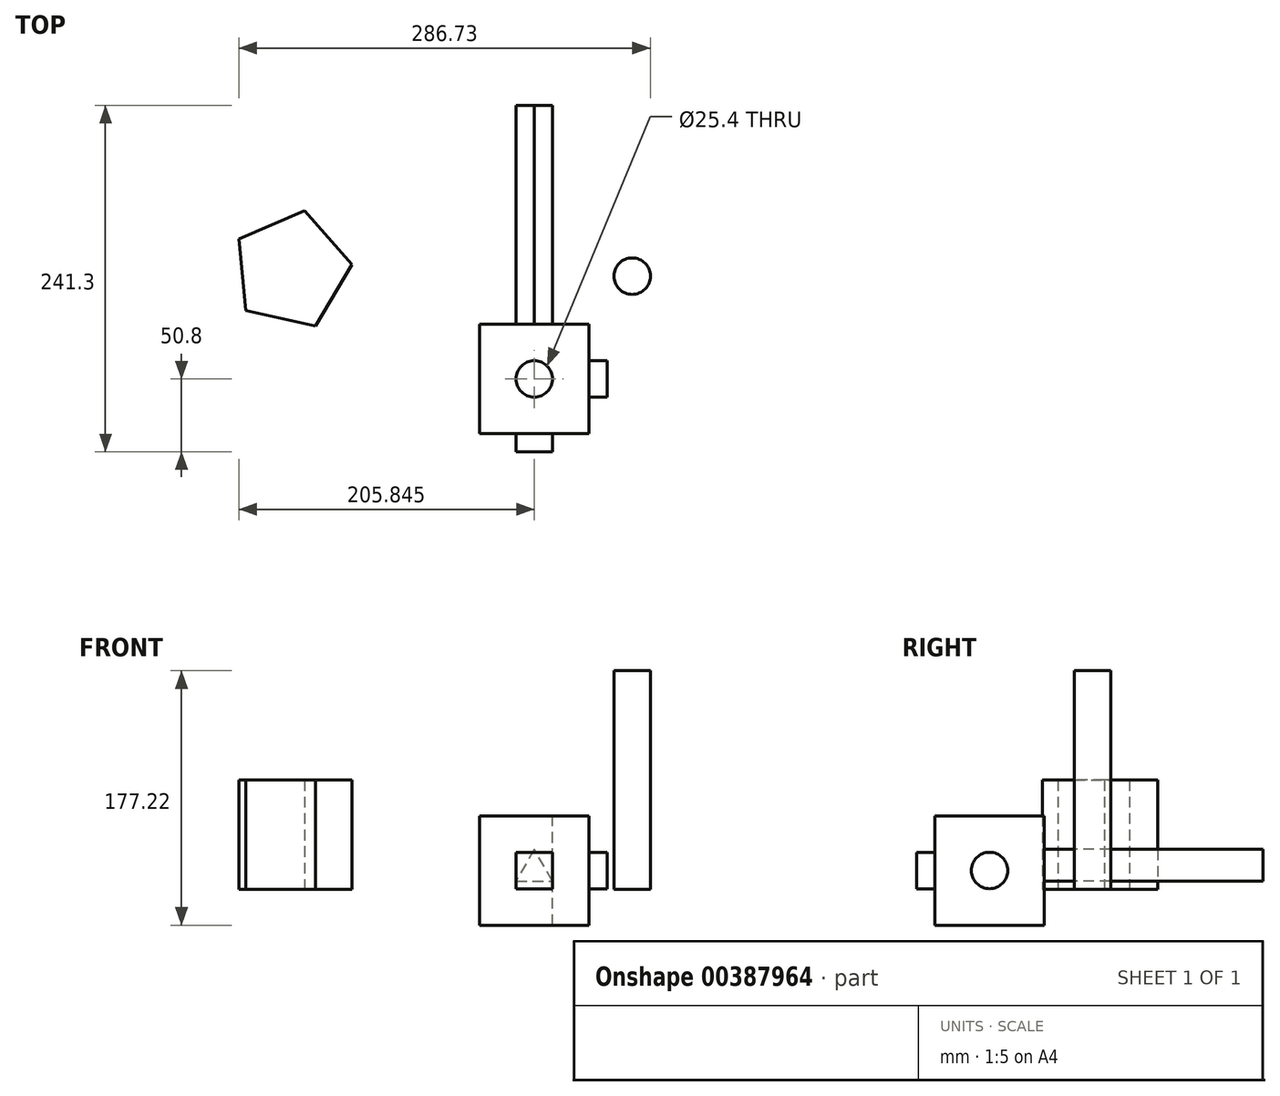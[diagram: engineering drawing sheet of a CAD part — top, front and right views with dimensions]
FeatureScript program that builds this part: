
annotation { "Feature Type Name" : "Feature", "Feature Type Description" : "" }
export const myFeature = defineFeature(function(context is Context, id is Id, definition is map)
    precondition{}
    {
        {
            var Q0;
            Q0=qCreatedBy(makeId("Front.planeOp"),FACE);
            var sketch = newSketch(context, id + "F0", { "sketchPlane" : qUnion([Q0])});
            skLineSegment(sketch, "E0.bottom", {"start": v(-38.89, -24.82) * mm, "end": v(37.31, -24.82) * mm});
            skLineSegment(sketch, "E0.top", {"start": v(-38.89, 51.38) * mm, "end": v(37.31, 51.38) * mm});
            skLineSegment(sketch, "E0.left", {"start": v(-38.89, -24.82) * mm, "end": v(-38.89, 51.38) * mm});
            skLineSegment(sketch, "E0.right", {"start": v(37.31, -24.82) * mm, "end": v(37.31, 51.38) * mm});
            skSolve(sketch);
        }
        {
            var Q0;
            Q0=makeQuery(id+"F0.imprint","IMPRINT",FACE,{"disambiguationData":[TD([[makeQuery(id+"F0.imprint","IMPRINT",EDGE,{"derivedFrom":sQuery(id+"F0.wireOp",EDGE,"E0.bottom")}),1.0]])]});
            extrude(context, id + "F1", {"entities" : qUnion([Q0]), "depth" : 76.2 * mm});
        }
        {
            var Q0;
            Q0=makeQuery(id+"F1.opExtrude","SWEPT_FACE",FACE,{"disambiguationData":[OSD([sQuery(id+"F0.wireOp",EDGE,"E0.top")])]});
            var sketch = newSketch(context, id + "F2", { "sketchPlane" : qUnion([Q0])});
            skPoint(sketch, "E1", {"position": v(-0.79, -38.1) * mm});
            skSolve(sketch);
        }
        {
            var Q0;
            Q0=sQuery(id+"F2.wireOp",VERTEX,"E1");
            var Q1;
            Q1=makeQuery(id+"F1.opExtrude","SWEPT_BODY",BODY,{"disambiguationData":[OSD([sQuery(id+"F0.wireOp",EDGE,"E0.bottom"),sQuery(id+"F0.wireOp",EDGE,"E0.top"),sQuery(id+"F0.wireOp",EDGE,"E0.left"),sQuery(id+"F0.wireOp",EDGE,"E0.right")])]});
            hole(context, id + "F3", {"style" : HoleStyle.SIMPLE, "endStyle" : HoleEndStyle.THROUGH, "holeDiameter" : 25.4 * mm, "isTappedThrough" : true, "tappedDepth" : 12.7 * mm, "tapClearance" : 3, "locations" : qUnion([Q0]), "scope" : qUnion([Q1])});
        }
        {
            var Q0;
            Q0=makeQuery(id+"F1.opExtrude","CAP_FACE",FACE,{"disambiguationData":[OSD([sQuery(id+"F0.wireOp",EDGE,"E0.bottom"),sQuery(id+"F0.wireOp",EDGE,"E0.top"),sQuery(id+"F0.wireOp",EDGE,"E0.left"),sQuery(id+"F0.wireOp",EDGE,"E0.right")])],"isStart":false});
            var sketch = newSketch(context, id + "F4", { "sketchPlane" : qUnion([Q0])});
            skLineSegment(sketch, "E2.bottom", {"start": v(-13.49, 0.58) * mm, "end": v(11.91, 0.58) * mm});
            skLineSegment(sketch, "E2.top", {"start": v(-13.49, 25.98) * mm, "end": v(11.91, 25.98) * mm});
            skLineSegment(sketch, "E2.left", {"start": v(-13.49, 0.58) * mm, "end": v(-13.49, 25.98) * mm});
            skLineSegment(sketch, "E2.right", {"start": v(11.91, 0.58) * mm, "end": v(11.91, 25.98) * mm});
            skSolve(sketch);
        }
        {
            var Q0;
            Q0=makeQuery(id+"F4.imprint","IMPRINT",FACE,{"disambiguationData":[TD([[makeQuery(id+"F4.imprint","IMPRINT",EDGE,{"derivedFrom":sQuery(id+"F4.wireOp",EDGE,"E2.bottom")}),1.0]])]});
            extrude(context, id + "F5", {"entities" : qUnion([Q0]), "operationType" : NewBodyOperationType.ADD, "depth" : 12.7 * mm});
        }
        {
            var Q0;
            Q0=makeQuery(id+"F1.opExtrude","SWEPT_FACE",FACE,{"disambiguationData":[OSD([sQuery(id+"F0.wireOp",EDGE,"E0.right")])]});
            var sketch = newSketch(context, id + "F6", { "sketchPlane" : qUnion([Q0])});
            skCircle(sketch, "E3", {"center": v(-38.1, 13.28) * mm, "radius": 12.7 * mm});
            skSolve(sketch);
        }
        {
            var Q0;
            Q0=makeQuery(id+"F6.imprint","IMPRINT",FACE,{"disambiguationData":[TD([[makeQuery(id+"F6.imprint","IMPRINT",EDGE,{"derivedFrom":sQuery(id+"F6.wireOp",EDGE,"E3")}),1.0]])]});
            extrude(context, id + "F7", {"entities" : qUnion([Q0]), "operationType" : NewBodyOperationType.ADD, "depth" : 12.7 * mm});
        }
        {
            var Q0;
            Q0=makeQuery(id+"F1.opExtrude","CAP_FACE",FACE,{"disambiguationData":[OSD([sQuery(id+"F0.wireOp",EDGE,"E0.bottom"),sQuery(id+"F0.wireOp",EDGE,"E0.top"),sQuery(id+"F0.wireOp",EDGE,"E0.left"),sQuery(id+"F0.wireOp",EDGE,"E0.right")])],"isStart":true});
            var sketch = newSketch(context, id + "F8", { "sketchPlane" : qUnion([Q0])});
            skCircle(sketch, "E4.cCircle", {"center": v(0.79, 13.28) * mm, "radius": 7.33 * mm, "construction": true});
            skLineSegment(sketch, "E4.0", {"start": v(-11.91, 5.95) * mm, "end": v(0.79, 27.94) * mm});
            skLineSegment(sketch, "E4.1", {"start": v(0.79, 27.94) * mm, "end": v(13.49, 5.95) * mm});
            skLineSegment(sketch, "E4.2", {"start": v(13.49, 5.95) * mm, "end": v(-11.91, 5.95) * mm});
            skPoint(sketch, "E4.0.midPoint", {"position": v(-5.56, 16.94) * mm});
            skSolve(sketch);
        }
        {
            var Q0;
            Q0=makeQuery(id+"F8.imprint","IMPRINT",FACE,{"disambiguationData":[TD([[makeQuery(id+"F8.imprint","IMPRINT",EDGE,{"derivedFrom":sQuery(id+"F8.wireOp",EDGE,"E4.0")}),-1.0]])]});
            extrude(context, id + "F9", {"entities" : qUnion([Q0]), "operationType" : NewBodyOperationType.ADD, "depth" : 152.4 * mm});
        }
        {
            var Q0;
            Q0=qCreatedBy(makeId("Top.planeOp"),FACE);
            var sketch = newSketch(context, id + "F10", { "sketchPlane" : qUnion([Q0])});
            skCircle(sketch, "E5", {"center": v(67.4, 33.52) * mm, "radius": 12.7 * mm});
            skSolve(sketch);
        }
        {
            var Q0;
            Q0=makeQuery(id+"F10.imprint","IMPRINT",FACE,{"disambiguationData":[TD([[makeQuery(id+"F10.imprint","IMPRINT",EDGE,{"derivedFrom":sQuery(id+"F10.wireOp",EDGE,"E5")}),1.0]])]});
            extrude(context, id + "F11", {"entities" : qUnion([Q0]), "depth" : 152.4 * mm});
        }
        {
            var Q0;
            Q0=qCreatedBy(makeId("Top.planeOp"),FACE);
            var sketch = newSketch(context, id + "F12", { "sketchPlane" : qUnion([Q0])});
            skCircle(sketch, "E6.cCircle", {"center": v(-170.1, 37.72) * mm, "radius": 34.33 * mm, "construction": true});
            skLineSegment(sketch, "E6.0", {"start": v(-127.84, 41.73) * mm, "end": v(-153.22, -1.22) * mm});
            skLineSegment(sketch, "E6.1", {"start": v(-153.22, -1.22) * mm, "end": v(-201.91, 9.64) * mm});
            skLineSegment(sketch, "E6.2", {"start": v(-201.91, 9.64) * mm, "end": v(-206.63, 59.3) * mm});
            skLineSegment(sketch, "E6.3", {"start": v(-206.63, 59.3) * mm, "end": v(-160.85, 79.14) * mm});
            skLineSegment(sketch, "E6.4", {"start": v(-160.85, 79.14) * mm, "end": v(-127.84, 41.73) * mm});
            skPoint(sketch, "E6.0.midPoint", {"position": v(-140.53, 20.26) * mm});
            skSolve(sketch);
        }
        {
            var Q0;
            Q0=makeQuery(id+"F12.imprint","IMPRINT",FACE,{"disambiguationData":[TD([[makeQuery(id+"F12.imprint","IMPRINT",EDGE,{"derivedFrom":sQuery(id+"F12.wireOp",EDGE,"E6.0")}),-1.0]])]});
            extrude(context, id + "F13", {"entities" : qUnion([Q0]), "depth" : 76.2 * mm});
        }
    });
